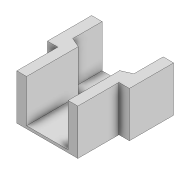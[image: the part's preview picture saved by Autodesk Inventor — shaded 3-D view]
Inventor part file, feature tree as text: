
AUTODESK INVENTOR PART (.ipt)
format: ipt  version: 2021 (Build 250183000, 183)  size: 132,608 bytes
history: native  units: in
note: dims shown in document units (in); Inventor stores cm internally (conversion verified against a paired STEP export)
features: extrude x3, sketch x3, projected_geometry x3
ambient origin geometry x8: Origin, YZ Plane, XZ Plane, XY Plane, X Axis, Y Axis, Z Axis, Center Point
bodies: Solid1 (feature_tree)
feature tree (9):
  extrude  "Extrusion1"  Depth=0.0625in TaperAngle=0.0deg
  extrude  "Extrusion2"  Depth=2.0in
  extrude  "Extrusion4"  [1 undecoded]
  sketch  "Sketch1"  dims[d0=1.0in d1=0.0in d2=0.0625in d3=0.0in]
  sketch  "Sketch2"  dims[d8=0.0625in d9=0.0in d10=2.0in]
  projected_geometry  "Projected Loop1"
  projected_geometry  "Projected Loop2"
  sketch  "Sketch4"  dims[d11=1.0in]
  projected_geometry  "Projected Loop4"
note: 1 required parameter value undecoded (feature->parameter linkage not recoverable at this tier; creation-order binding heuristic only, values carry confidence <= 0.55)
